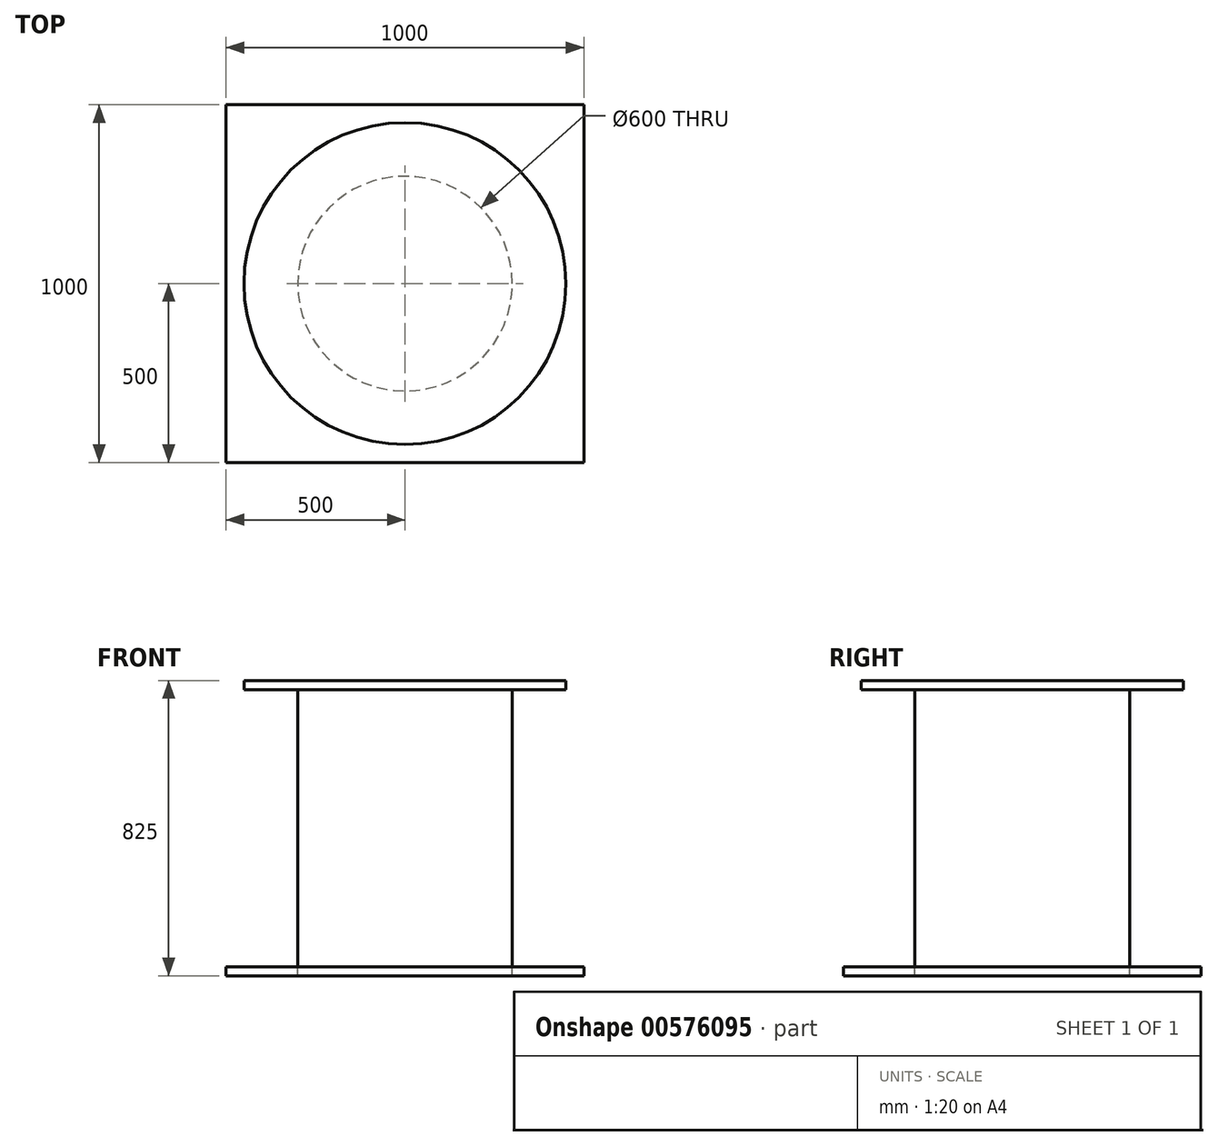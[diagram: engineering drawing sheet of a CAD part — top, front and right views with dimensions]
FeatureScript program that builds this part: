
annotation { "Feature Type Name" : "Feature", "Feature Type Description" : "" }
export const myFeature = defineFeature(function(context is Context, id is Id, definition is map)
    precondition{}
    {
        {
            var Q0;
            Q0=qCreatedBy(makeId("Top.planeOp"),FACE);
            var sketch = newSketch(context, id + "F0", { "sketchPlane" : qUnion([Q0])});
            skCircle(sketch, "E0", {"center": v(0, 0) * mm, "radius": 450 * mm});
            skSolve(sketch);
        }
        {
            var Q0;
            Q0=makeQuery(id+"F0.imprint","IMPRINT",FACE,{"disambiguationData":[TD([[makeQuery(id+"F0.imprint","IMPRINT",EDGE,{"derivedFrom":sQuery(id+"F0.wireOp",EDGE,"E0")}),1.0]])]});
            extrude(context, id + "F1", {"entities" : qUnion([Q0]), "depth" : 25 * mm, "offsetDistance" : 25 * mm});
        }
        {
            var Q0;
            Q0=makeQuery(id+"F1.opExtrude","CAP_FACE",FACE,{"disambiguationData":[OSD([sQuery(id+"F0.wireOp",EDGE,"E0")])],"isStart":false});
            var sketch = newSketch(context, id + "F2", { "sketchPlane" : qUnion([Q0])});
            skCircle(sketch, "E1", {"center": v(0, 0) * mm, "radius": 300 * mm});
            skSolve(sketch);
        }
        {
            var Q0;
            Q0=makeQuery(id+"F2.imprint","IMPRINT",FACE,{"disambiguationData":[TD([[makeQuery(id+"F2.imprint","IMPRINT",EDGE,{"derivedFrom":sQuery(id+"F2.wireOp",EDGE,"E1")}),1.0]])]});
            extrude(context, id + "F3", {"entities" : qUnion([Q0]), "operationType" : NewBodyOperationType.ADD, "oppositeDirection" : true, "depth" : 800 * mm, "offsetDistance" : 25 * mm});
        }
        {
            var Q0;
            Q0=makeQuery(id+"F3.opExtrude","CAP_FACE",FACE,{"disambiguationData":[OSD([sQuery(id+"F2.wireOp",EDGE,"E1")])],"isStart":false});
            var sketch = newSketch(context, id + "F4", { "sketchPlane" : qUnion([Q0])});
            skLineSegment(sketch, "E2.bottom", {"start": v(500, 500) * mm, "end": v(-500, 500) * mm});
            skLineSegment(sketch, "E2.top", {"start": v(500, -500) * mm, "end": v(-500, -500) * mm});
            skLineSegment(sketch, "E2.left", {"start": v(500, 500) * mm, "end": v(500, -500) * mm});
            skLineSegment(sketch, "E2.right", {"start": v(-500, 500) * mm, "end": v(-500, -500) * mm});
            skPoint(sketch, "E2.middle", {"position": v(0, 0) * mm});
            skSolve(sketch);
        }
        {
            var Q0;
            Q0=makeQuery(id+"F4.imprint","IMPRINT",FACE,{"disambiguationData":[TD([[makeQuery(id+"F4.imprint","IMPRINT",EDGE,{"derivedFrom":sQuery(id+"F4.wireOp",EDGE,"E2.bottom")}),1.0]])]});
            extrude(context, id + "F5", {"entities" : qUnion([Q0]), "depth" : 25 * mm, "offsetDistance" : 25 * mm});
        }
    });
